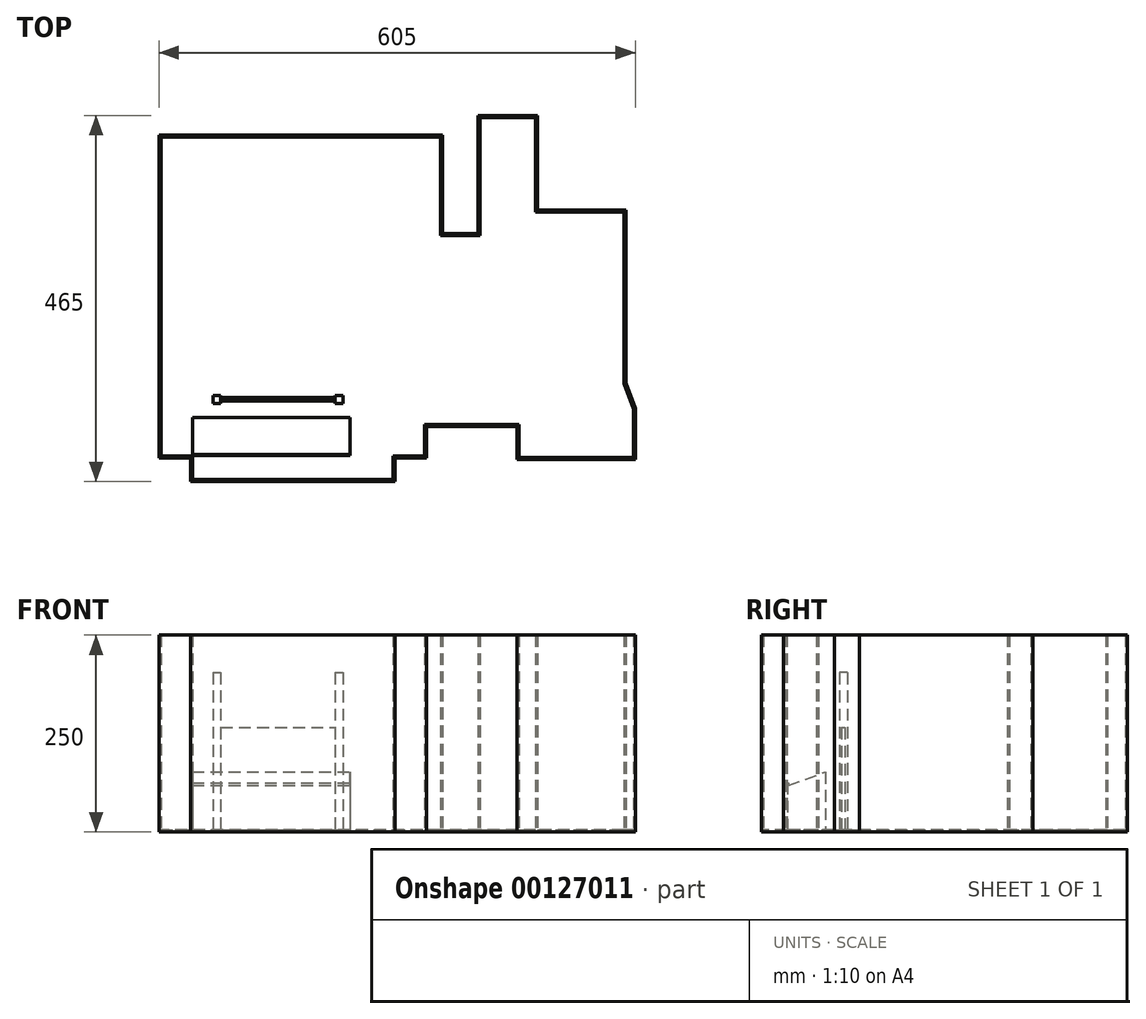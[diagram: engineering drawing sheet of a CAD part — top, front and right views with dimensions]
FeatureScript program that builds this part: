
annotation { "Feature Type Name" : "Feature", "Feature Type Description" : "" }
export const myFeature = defineFeature(function(context is Context, id is Id, definition is map)
    precondition{}
    {
        {
            var Q0;
            Q0=qCreatedBy(makeId("Top.planeOp"),FACE);
            var sketch = newSketch(context, id + "F0", { "sketchPlane" : qUnion([Q0])});
            skLineSegment(sketch, "E0", {"start": v(-255.32, 230.65) * mm, "end": v(-255.32, -179.35) * mm});
            skLineSegment(sketch, "E1", {"start": v(-215.32, -179.35) * mm, "end": v(-215.32, -209.35) * mm});
            skLineSegment(sketch, "E2", {"start": v(-215.32, -209.35) * mm, "end": v(44.68, -209.35) * mm});
            skLineSegment(sketch, "E3", {"start": v(44.68, -209.35) * mm, "end": v(44.68, -179.35) * mm});
            skLineSegment(sketch, "E4", {"start": v(44.68, -179.35) * mm, "end": v(84.68, -179.35) * mm});
            skLineSegment(sketch, "E5", {"start": v(84.68, -179.35) * mm, "end": v(84.68, -139.35) * mm});
            skLineSegment(sketch, "E6", {"start": v(84.68, -139.35) * mm, "end": v(199.68, -139.35) * mm});
            skLineSegment(sketch, "E7", {"start": v(199.68, -139.35) * mm, "end": v(199.68, -181.35) * mm});
            skLineSegment(sketch, "E8", {"start": v(199.68, -181.35) * mm, "end": v(349.68, -181.35) * mm});
            skLineSegment(sketch, "E9", {"start": v(349.68, -181.35) * mm, "end": v(349.68, -116.35) * mm});
            skLineSegment(sketch, "E10", {"start": v(349.68, -116.35) * mm, "end": v(337.68, -84.35) * mm});
            skLineSegment(sketch, "E11", {"start": v(337.68, -84.35) * mm, "end": v(337.68, 135.65) * mm});
            skLineSegment(sketch, "E12", {"start": v(337.68, 135.65) * mm, "end": v(225.68, 135.65) * mm});
            skLineSegment(sketch, "E13", {"start": v(225.68, 135.65) * mm, "end": v(225.68, 255.65) * mm});
            skLineSegment(sketch, "E14", {"start": v(225.68, 255.65) * mm, "end": v(149.68, 255.65) * mm});
            skLineSegment(sketch, "E15", {"start": v(149.68, 255.65) * mm, "end": v(149.68, 105.65) * mm});
            skLineSegment(sketch, "E16", {"start": v(149.68, 105.65) * mm, "end": v(104.68, 105.65) * mm});
            skLineSegment(sketch, "E17", {"start": v(104.68, 105.65) * mm, "end": v(104.68, 230.65) * mm});
            skLineSegment(sketch, "E18", {"start": v(104.68, 230.65) * mm, "end": v(-255.32, 230.65) * mm});
            skLineSegment(sketch, "E19", {"start": v(-255.32, -179.35) * mm, "end": v(-215.32, -179.35) * mm});
            skSolve(sketch);
        }
        {
            var Q0;
            Q0 = qSketchRegion(id + "F0", true);
            extrude(context, id + "F1", {"entities" : qUnion([Q0]), "depth" : 250 * mm});
        }
        {
            var Q0;
            Q0=makeQuery(id+"F1.opExtrude","CAP_FACE",FACE,{"disambiguationData":[OSD([sQuery(id+"F0.wireOp",EDGE,"E0"),sQuery(id+"F0.wireOp",EDGE,"E1"),sQuery(id+"F0.wireOp",EDGE,"E2"),sQuery(id+"F0.wireOp",EDGE,"E3"),sQuery(id+"F0.wireOp",EDGE,"E4"),sQuery(id+"F0.wireOp",EDGE,"E5"),sQuery(id+"F0.wireOp",EDGE,"E6"),sQuery(id+"F0.wireOp",EDGE,"E7"),sQuery(id+"F0.wireOp",EDGE,"E8"),sQuery(id+"F0.wireOp",EDGE,"E9"),sQuery(id+"F0.wireOp",EDGE,"E10"),sQuery(id+"F0.wireOp",EDGE,"E11"),sQuery(id+"F0.wireOp",EDGE,"E12"),sQuery(id+"F0.wireOp",EDGE,"E13"),sQuery(id+"F0.wireOp",EDGE,"E14"),sQuery(id+"F0.wireOp",EDGE,"E15"),sQuery(id+"F0.wireOp",EDGE,"E16"),sQuery(id+"F0.wireOp",EDGE,"E17"),sQuery(id+"F0.wireOp",EDGE,"E18"),sQuery(id+"F0.wireOp",EDGE,"E19")])],"isStart":false});
            shell(context, id + "F2", {"entities" : qUnion([Q0]), "thickness" : 2.5 * mm});
        }
        {
            var Q0;
            Q0=makeQuery(id+"F2.opShell","OFFSET_FACE",FACE,{"disambiguationData":[OSD([sQuery(id+"F0.wireOp",EDGE,"E0"),sQuery(id+"F0.wireOp",EDGE,"E1"),sQuery(id+"F0.wireOp",EDGE,"E2"),sQuery(id+"F0.wireOp",EDGE,"E3"),sQuery(id+"F0.wireOp",EDGE,"E4"),sQuery(id+"F0.wireOp",EDGE,"E5"),sQuery(id+"F0.wireOp",EDGE,"E6"),sQuery(id+"F0.wireOp",EDGE,"E7"),sQuery(id+"F0.wireOp",EDGE,"E8"),sQuery(id+"F0.wireOp",EDGE,"E9"),sQuery(id+"F0.wireOp",EDGE,"E10"),sQuery(id+"F0.wireOp",EDGE,"E11"),sQuery(id+"F0.wireOp",EDGE,"E12"),sQuery(id+"F0.wireOp",EDGE,"E13"),sQuery(id+"F0.wireOp",EDGE,"E14"),sQuery(id+"F0.wireOp",EDGE,"E15"),sQuery(id+"F0.wireOp",EDGE,"E16"),sQuery(id+"F0.wireOp",EDGE,"E17"),sQuery(id+"F0.wireOp",EDGE,"E18"),sQuery(id+"F0.wireOp",EDGE,"E19")])]});
            var sketch = newSketch(context, id + "F3", { "sketchPlane" : qUnion([Q0])});
            skLineSegment(sketch, "E20.bottom", {"start": v(-212.82, -176.26) * mm, "end": v(-12.82, -176.26) * mm});
            skLineSegment(sketch, "E20.top", {"start": v(-212.82, -174.76) * mm, "end": v(-12.82, -174.76) * mm});
            skLineSegment(sketch, "E20.left", {"start": v(-212.82, -176.26) * mm, "end": v(-212.82, -174.76) * mm});
            skLineSegment(sketch, "E20.right", {"start": v(-12.82, -176.26) * mm, "end": v(-12.82, -174.76) * mm});
            skSolve(sketch);
        }
        {
            var Q0;
            Q0 = qSketchRegion(id + "F3", true);
            extrude(context, id + "F4", {"entities" : qUnion([Q0]), "operationType" : NewBodyOperationType.ADD, "depth" : 60 * mm});
        }
        {
            var Q0;
            Q0=makeQuery(id+"F4.opExtrude","SWEPT_FACE",FACE,{"disambiguationData":[OSD([sQuery(id+"F3.wireOp",EDGE,"E20.right")])]});
            var sketch = newSketch(context, id + "F5", { "sketchPlane" : qUnion([Q0])});
            skLineSegment(sketch, "E21", {"start": v(-174.76, 59.07) * mm, "end": v(-127.78, 76.18) * mm});
            skLineSegment(sketch, "E22", {"start": v(-127.78, 76.18) * mm, "end": v(-127.78, 2.5) * mm});
            skLineSegment(sketch, "E23", {"start": v(-127.78, 2.5) * mm, "end": v(-174.76, 2.5) * mm});
            skLineSegment(sketch, "E24", {"start": v(-174.76, 2.5) * mm, "end": v(-174.76, 59.07) * mm});
            skSolve(sketch);
        }
        {
            var Q0;
            Q0 = qSketchRegion(id + "F5", true);
            extrude(context, id + "F6", {"entities" : qUnion([Q0]), "operationType" : NewBodyOperationType.ADD, "oppositeDirection" : true, "depth" : 200 * mm});
        }
        {
            var Q0;
            Q0=makeQuery(id+"F2.opShell","OFFSET_FACE",FACE,{"disambiguationData":[OSD([sQuery(id+"F0.wireOp",EDGE,"E0"),sQuery(id+"F0.wireOp",EDGE,"E1"),sQuery(id+"F0.wireOp",EDGE,"E2"),sQuery(id+"F0.wireOp",EDGE,"E3"),sQuery(id+"F0.wireOp",EDGE,"E4"),sQuery(id+"F0.wireOp",EDGE,"E5"),sQuery(id+"F0.wireOp",EDGE,"E6"),sQuery(id+"F0.wireOp",EDGE,"E7"),sQuery(id+"F0.wireOp",EDGE,"E8"),sQuery(id+"F0.wireOp",EDGE,"E9"),sQuery(id+"F0.wireOp",EDGE,"E10"),sQuery(id+"F0.wireOp",EDGE,"E11"),sQuery(id+"F0.wireOp",EDGE,"E12"),sQuery(id+"F0.wireOp",EDGE,"E13"),sQuery(id+"F0.wireOp",EDGE,"E14"),sQuery(id+"F0.wireOp",EDGE,"E15"),sQuery(id+"F0.wireOp",EDGE,"E16"),sQuery(id+"F0.wireOp",EDGE,"E17"),sQuery(id+"F0.wireOp",EDGE,"E18"),sQuery(id+"F0.wireOp",EDGE,"E19")])]});
            var sketch = newSketch(context, id + "F7", { "sketchPlane" : qUnion([Q0])});
            skLineSegment(sketch, "E25.bottom", {"start": v(-186.84, -100.2) * mm, "end": v(-176.84, -100.2) * mm});
            skLineSegment(sketch, "E25.top", {"start": v(-186.84, -110.2) * mm, "end": v(-176.84, -110.2) * mm});
            skLineSegment(sketch, "E25.left", {"start": v(-186.84, -100.2) * mm, "end": v(-186.84, -110.2) * mm});
            skLineSegment(sketch, "E25.right", {"start": v(-176.84, -100.2) * mm, "end": v(-176.84, -110.2) * mm});
            skLineSegment(sketch, "E26.bottom", {"start": v(-31.84, -110.2) * mm, "end": v(-21.84, -110.2) * mm});
            skLineSegment(sketch, "E26.top", {"start": v(-31.84, -100.2) * mm, "end": v(-21.84, -100.2) * mm});
            skLineSegment(sketch, "E26.left", {"start": v(-31.84, -110.2) * mm, "end": v(-31.84, -100.2) * mm});
            skLineSegment(sketch, "E26.right", {"start": v(-21.84, -110.2) * mm, "end": v(-21.84, -100.2) * mm});
            skLineSegment(sketch, "E27.bottom", {"start": v(-176.84, -102.75) * mm, "end": v(-31.84, -102.75) * mm});
            skLineSegment(sketch, "E27.top", {"start": v(-176.84, -107.2) * mm, "end": v(-31.84, -107.2) * mm});
            skLineSegment(sketch, "E27.left", {"start": v(-176.84, -102.75) * mm, "end": v(-176.84, -107.2) * mm});
            skLineSegment(sketch, "E27.right", {"start": v(-31.84, -102.75) * mm, "end": v(-31.84, -107.2) * mm});
            skSolve(sketch);
        }
        {
            var Q0;
            {var subQ1=sQuery(id+"F7.wireOp",EDGE,"E25.bottom");Q0=makeQuery(id+"F7.imprint","IMPRINT",FACE,{"disambiguationData":[TD([[makeQuery(id+"F7.imprint","IMPRINT",EDGE,{"derivedFrom":subQ1}),-1.0]])]});}
            var Q1;
            {var subQ3=sQuery(id+"F7.wireOp",EDGE,"E26.bottom");Q1=makeQuery(id+"F7.imprint","IMPRINT",FACE,{"disambiguationData":[TD([[makeQuery(id+"F7.imprint","IMPRINT",EDGE,{"derivedFrom":subQ3}),1.0]])]});}
            extrude(context, id + "F8", {"entities" : qUnion([Q0, Q1]), "depth" : 200 * mm});
        }
        {
            var Q0;
            Q0=makeQuery(id+"F7.imprint","IMPRINT",FACE,{"disambiguationData":[TD([[makeQuery(id+"F7.imprint","IMPRINT",EDGE,{"derivedFrom":sQuery(id+"F7.wireOp",EDGE,"E27.bottom")}),-1.0]])]});
            extrude(context, id + "F9", {"entities" : qUnion([Q0]), "depth" : 130 * mm});
        }
    });
